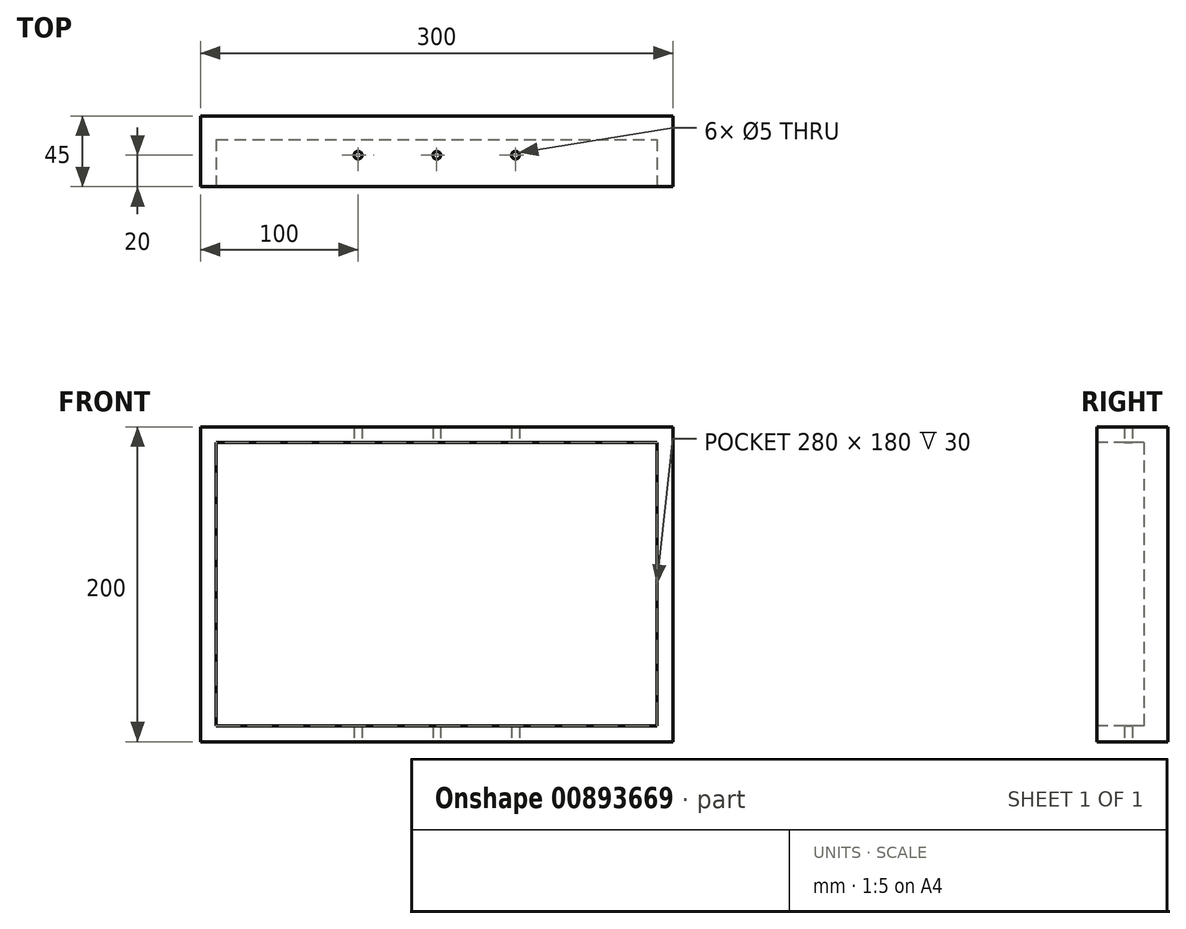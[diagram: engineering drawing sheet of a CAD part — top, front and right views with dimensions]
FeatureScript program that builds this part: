
annotation { "Feature Type Name" : "Feature", "Feature Type Description" : "" }
export const myFeature = defineFeature(function(context is Context, id is Id, definition is map)
    precondition{}
    {
        {
            var Q0;
            Q0=qCreatedBy(makeId("Front.planeOp"),FACE);
            var sketch = newSketch(context, id + "F0", { "sketchPlane" : qUnion([Q0])});
            skLineSegment(sketch, "E0.bottom", {"start": v(-150, 100) * mm, "end": v(150, 100) * mm});
            skLineSegment(sketch, "E0.top", {"start": v(-150, -100) * mm, "end": v(150, -100) * mm});
            skLineSegment(sketch, "E0.left", {"start": v(-150, 100) * mm, "end": v(-150, -100) * mm});
            skLineSegment(sketch, "E0.right", {"start": v(150, 100) * mm, "end": v(150, -100) * mm});
            skSolve(sketch);
        }
        {
            var Q0;
            Q0 = qSketchRegion(id + "F0", true);
            extrude(context, id + "F1", {"entities" : qUnion([Q0]), "depth" : 45 * mm, "offsetDistance" : 25 * mm});
        }
        {
            var Q0;
            Q0=makeQuery(id+"F1.opExtrude","CAP_FACE",FACE,{"disambiguationData":[OSD([sQuery(id+"F0.wireOp",EDGE,"E0.bottom"),sQuery(id+"F0.wireOp",EDGE,"E0.top"),sQuery(id+"F0.wireOp",EDGE,"E0.left"),sQuery(id+"F0.wireOp",EDGE,"E0.right")])],"isStart":false});
            var sketch = newSketch(context, id + "F2", { "sketchPlane" : qUnion([Q0])});
            skLineSegment(sketch, "E1.bottom", {"start": v(-140, 90) * mm, "end": v(140, 90) * mm});
            skLineSegment(sketch, "E1.top", {"start": v(-140, -90) * mm, "end": v(140, -90) * mm});
            skLineSegment(sketch, "E1.left", {"start": v(-140, 90) * mm, "end": v(-140, -90) * mm});
            skLineSegment(sketch, "E1.right", {"start": v(140, 90) * mm, "end": v(140, -90) * mm});
            skSolve(sketch);
        }
        {
            var Q0;
            Q0 = qSketchRegion(id + "F2", true);
            extrude(context, id + "F3", {"entities" : qUnion([Q0]), "operationType" : NewBodyOperationType.REMOVE, "oppositeDirection" : true, "depth" : 30 * mm, "offsetDistance" : 25 * mm});
        }
        {
            var Q0;
            Q0=makeQuery(id+"F1.opExtrude","SWEPT_FACE",FACE,{"disambiguationData":[OSD([sQuery(id+"F0.wireOp",EDGE,"E0.top")])]});
            var sketch = newSketch(context, id + "F4", { "sketchPlane" : qUnion([Q0])});
            skCircle(sketch, "E2", {"center": v(-50, 25) * mm, "radius": 2.5 * mm});
            skCircle(sketch, "E3", {"center": v(0, 25) * mm, "radius": 2.5 * mm});
            skCircle(sketch, "E4", {"center": v(50, 25) * mm, "radius": 2.5 * mm});
            skSolve(sketch);
        }
        {
            var Q0;
            Q0 = qSketchRegion(id + "F4", true);
            extrude(context, id + "F5", {"entities" : qUnion([Q0]), "operationType" : NewBodyOperationType.REMOVE, "endBound" : BoundingType.THROUGH_ALL, "oppositeDirection" : true, "depth" : 25 * mm, "offsetDistance" : 25 * mm});
        }
    });
